# Revit family: Drain_Floor_Shallow-Type_Round_Zurn-Z1730_Heavy-Duty
name_source: partatom
category: Plumbing Fixtures
units: mm (PartAtom-declared; Revit-internal decimal feet)

## family parameters
Always vertical = Yes
Cut with Voids When Loaded = No
Maintain Annotation Orientation = No
OmniClass Number = 23.45.55.21
OmniClass Title = Drains (Wastes)
Part Type = Normal
Room Calculation Point = No
Round Connector Dimension = Use Radius
Shared = No
Work Plane-Based = No

## types (18) — shared parameters
Approx. Weight (Lbs) = 20 "
Assembly Code = D2030300
Body HT Dim 'E' = 4.813 "
CW Connection = No
Description = 9 INCH DIAMETER FLOOR DRAIN SHALLOW TYPE
HW Connection = No
Manufacturer = Zurn Water, LLC
Manufacurer Brand = Zurn
Modified Date = 10/31/25
Product Documentation Link = https://files.zurn.com
Product Page URL = https://www.zurn.com
Product data url = https://www.bimobject.com
URL = www.zurn.com
Vent Connection = No
Waste Connection = Yes
zero-valued in all types: CWFU, Default Elevation, HWFU, WFU

## per-type parameters (varying)
| type | Main Material | Model | Pipe Size 'A' (Inner Diameter) | Pipe Size 'A' (Inner Radius) | Pipe Size 'A' (Nominal Diameter) | Pipe Size 'A' (Nominal Radius) | Pipe Size 'A' (Outer Diameter) | Pipe Size 'A' (Outer Radius) | Type Comments |
| Z1730-2BW | Steel - Zurn- Stainless - Type - 304 | Z1730 | 2.067 " | 1.034 " | 2 " | 1 " | 2.375 " | 1.188 " | Z1730 - 2 inch Butt-Weld Outlet |
| Z1730-3BW | Steel - Zurn- Stainless - Type - 304 | Z1730 | 3.068 " | 1.534 " | 3 " | 1.5 " | 3.5 " | 1.75 " | Z1730 - 3 inch Butt-Weld Outlet |
| Z1730-4BW | Steel - Zurn- Stainless - Type - 304 | Z1730 | 4.026 " | 2.013 " | 4 " | 2 " | 4.5 " | 2.25 " | Z1730 - 4 inch Butt-Weld Outlet |
| Z1730-2NH | Steel - Zurn- Stainless - Type - 304 | Z1730 | 2.067 " | 1.034 " | 2 " | 1 " | 2.375 " | 1.188 " | Z1730 - 2 inch No-Hub Outlet |
| Z1730-3NH | Steel - Zurn- Stainless - Type - 304 | Z1730 | 3.068 " | 1.534 " | 3 " | 1.5 " | 3.5 " | 1.75 " | Z1730 - 3 inch No-Hub Outlet |
| Z1730-4NH | Steel - Zurn- Stainless - Type - 304 | Z1730 | 4.026 " | 2.013 " | 4 " | 2 " | 4.5 " | 2.25 " | Z1730 - 4 inch No-Hub Outlet |
| Z1730-2IP | Steel - Zurn- Stainless - Type - 304 | Z1730 | 2.067 " | 1.034 " | 2 " | 1 " | 2.375 " | 1.188 " | Z1730 - 2 inch IP Threaded Outlet |
| Z1730-3IP | Steel - Zurn- Stainless - Type - 304 | Z1730 | 3.068 " | 1.534 " | 3 " | 1.5 " | 3.5 " | 1.75 " | Z1730 - 3 inch IP Threaded Outlet |
| Z1730-4IP | Steel - Zurn- Stainless - Type - 304 | Z1730 | 4.026 " | 2.013 " | 4 " | 2 " | 4.5 " | 2.25 " | Z1730 - 4 inch IP Threaded Outlet |
| ZM1730-2BW | Steel - Zurn- Stainless - Type - 316 | ZM1730 | 2.067 " | 1.034 " | 2 " | 1 " | 2.375 " | 1.188 " | ZM1730 - 2 inch Butt-Weld Outlet |
| ZM1730-3BW | Steel - Zurn- Stainless - Type - 316 | ZM1730 | 3.068 " | 1.534 " | 3 " | 1.5 " | 3.5 " | 1.75 " | ZM1730 - 3 inch Butt-Weld Outlet |
| ZM1730-4BW | Steel - Zurn- Stainless - Type - 316 | ZM1730 | 4.026 " | 2.013 " | 4 " | 2 " | 4.5 " | 2.25 " | ZM1730 - 4 inch Butt-Weld Outlet |
| ZM1730-2NH | Steel - Zurn- Stainless - Type - 316 | ZM1730 | 2.067 " | 1.034 " | 2 " | 1 " | 2.375 " | 1.188 " | ZM1730 - 2 inch No-Hub Outlet |
| ZM1730-3NH | Steel - Zurn- Stainless - Type - 316 | ZM1730 | 3.068 " | 1.534 " | 3 " | 1.5 " | 3.5 " | 1.75 " | ZM1730 - 3 inch No-Hub Outlet |
| ZM1730-4NH | Steel - Zurn- Stainless - Type - 316 | ZM1730 | 4.026 " | 2.013 " | 4 " | 2 " | 4.5 " | 2.25 " | ZM1730 - 4 inch No-Hub Outlet |
| ZM1730-2IP | Steel - Zurn- Stainless - Type - 316 | ZM1730 | 2.067 " | 1.034 " | 2 " | 1 " | 2.375 " | 1.188 " | ZM1730 - 2 inch IP Threaded Outlet |
| ZM1730-3IP | Steel - Zurn- Stainless - Type - 316 | ZM1730 | 3.068 " | 1.534 " | 3 " | 1.5 " | 3.5 " | 1.75 " | ZM1730 - 3 inch IP Threaded Outlet |
| ZM1730-4IP | Steel - Zurn- Stainless - Type - 316 | ZM1730 | 4.026 " | 2.013 " | 4 " | 2 " | 4.5 " | 2.25 " | ZM1730 - 4 inch IP Threaded Outlet |

## geometry (parser evidence)
native form markers: Sweep x4
no freeform markers — native parametric forms only
